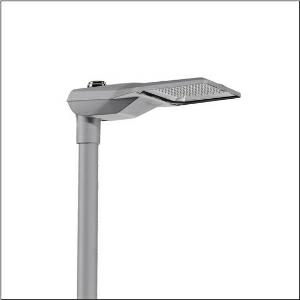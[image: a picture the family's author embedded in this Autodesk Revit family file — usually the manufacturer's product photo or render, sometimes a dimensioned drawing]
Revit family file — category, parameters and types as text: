
# Revit family: streetlight_sl_21_midi___stw1_0a_5xe7e37n08mb_6d50
name_source: partatom
category: Lighting Fixtures
units: mm (PartAtom-declared; Revit-internal decimal feet)

## family parameters
Cut with Voids When Loaded = No
Host = Face
Light Source = No
Part Type = Normal
Room Calculation Point = No
Round Connector Dimension = Use Diameter
Shared = No

## types (1)
- --- (1 x LED, 18270 lm, 136 W, 3000K)
    Apparent Load = 136 VA
    CIE Flux Codes = 38 75 98 100 100
    Color Rendering = 70
    Color Temperature = 3000K
    Default Elevation = 1800 mm
    Description = Streetlight SL 21 midi, mast luminaire, primary light control with lens, of PMMA, primary optical cover: cover, of toughened safety glass, transparent, light distribution: STW1.0a, light emission: direct distribution, primary light characteristic: asymmetric, installation type: side-entry, LED, 3G 2.5mm², High Power LED, rated luminous flux: 18.270lm, luminous efficacy: 134lm/W, light colour: 730, colour temperature: 3000K, control gear: NEMA (7pin), control: overheat protection, pre-setting: linear dimming characteristic, constant luminous flux control, time-dependent luminous flux control, flexible luminous flux parameterisation, mains connection: 220..240V, AC, 50/60Hz, connection cable pre-assembled, cable length: 12,5m, wiring characteristics: H05VV-F, start of lifetime: 136W, end of service life: 142W, reduction: 61W, luminaire housing, of diecast aluminium (EN AC-44300), powder-coated, SITECO metallic grey (DB 702S), corrosivity category C5 high according to DIN EN ISO 12944, multi-level sealing system, sealing non-destructively replaceable, inclination adjustable: 0°, 5°, 10°, 15°, length: 644mm, width: 335mm, height: 110mm, spigot size: 42mm (side-entry), mounting height: 4..8m, protection rating (complete): IP66, insulation class (complete): insulation class I (protective earthing), certification: CE, ENEC, ENEC+, VDE, impact resistance: IK10, permissible operating ambient temperature for outdoor applications: -40..+50°C, standard-compliant lighting for roads and squares, packaging unit: 1 piece

Light Distribution: STW1.0a
    Height = 111 mm
    Lamp = 1 x LED
    Lamp Light Flux = 18270 lm
    Lamp Power = 136 W
    Lamp count = 1
    Length = 644 mm
    Luminous efficacy = 134 lm/W
    Manufacturer = Siteco
    ModVariant = No
    Model = 5XE7E37N08MB
    Number of Poles = 1
    OnlyDefault = Yes
    Power Factor = 1
    Product Name = Streetlight SL 21 midi | STW1.0a
    Product group = mast luminaire | pylon top
    ProductGroupID = 6100
    Protection Class = Protection class I
    Protection Degree = IP 66
    RLX_Detail_Level = 1
    RLX_Emergency_Light_Flux = 0 lm
    RLX_Emergency_Type = 0
    RLX_Emergency_Type_DB = No
    RlxData = <blob elided: 26525 chars, md5=368a1750>
    Socket = socket
    Standby Power = 0 W
    System Light Flux = 18270 lm
    System Power = 136 W
    Type Comments = factory setting: luminous flux: 100 % | dim-lin: 254 | 695 mA
    Type Image = l_1294377.jpg
    URL = http://relux.com
    VarID = @adj_135015
    Voltage = 0 V
    Weight = 0.00 kg
    Width = 336 mm

## geometry (parser evidence)
native form markers: Blend x4, Sweep x10
no freeform markers — native parametric forms only
